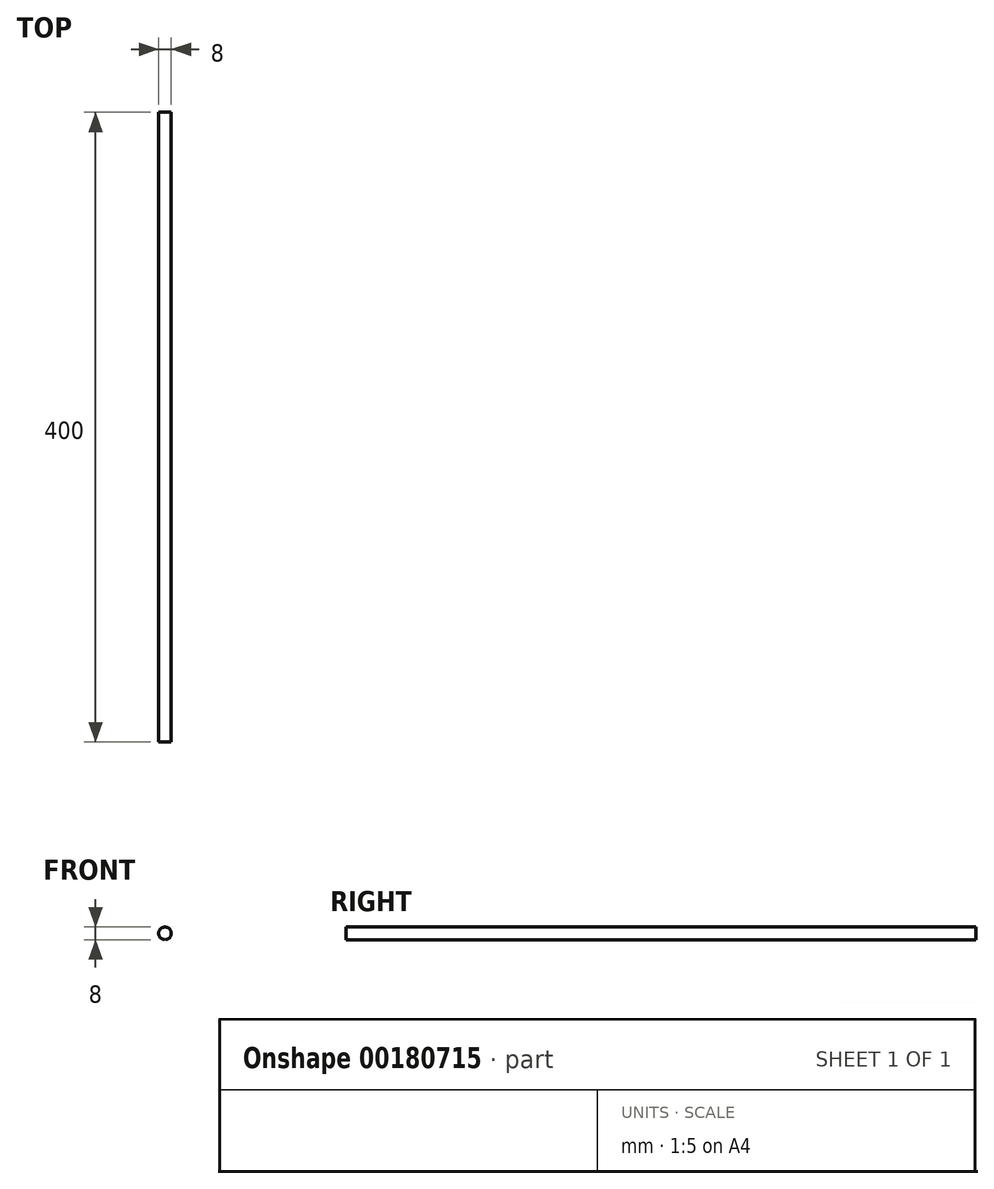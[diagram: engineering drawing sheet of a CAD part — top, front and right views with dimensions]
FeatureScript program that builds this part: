
annotation { "Feature Type Name" : "Feature", "Feature Type Description" : "" }
export const myFeature = defineFeature(function(context is Context, id is Id, definition is map)
    precondition{}
    {
        {
            var Q0;
            Q0=qCreatedBy(makeId("Front.planeOp"),FACE);
            var sketch = newSketch(context, id + "F0", { "sketchPlane" : qUnion([Q0])});
            skCircle(sketch, "E0", {"center": v(0, 0) * mm, "radius": 4 * mm});
            skSolve(sketch);
        }
        {
            var Q0;
            Q0 = qSketchRegion(id + "F0", true);
            extrude(context, id + "F1", {"entities" : qUnion([Q0]), "depth" : 400 * mm});
        }
    });
